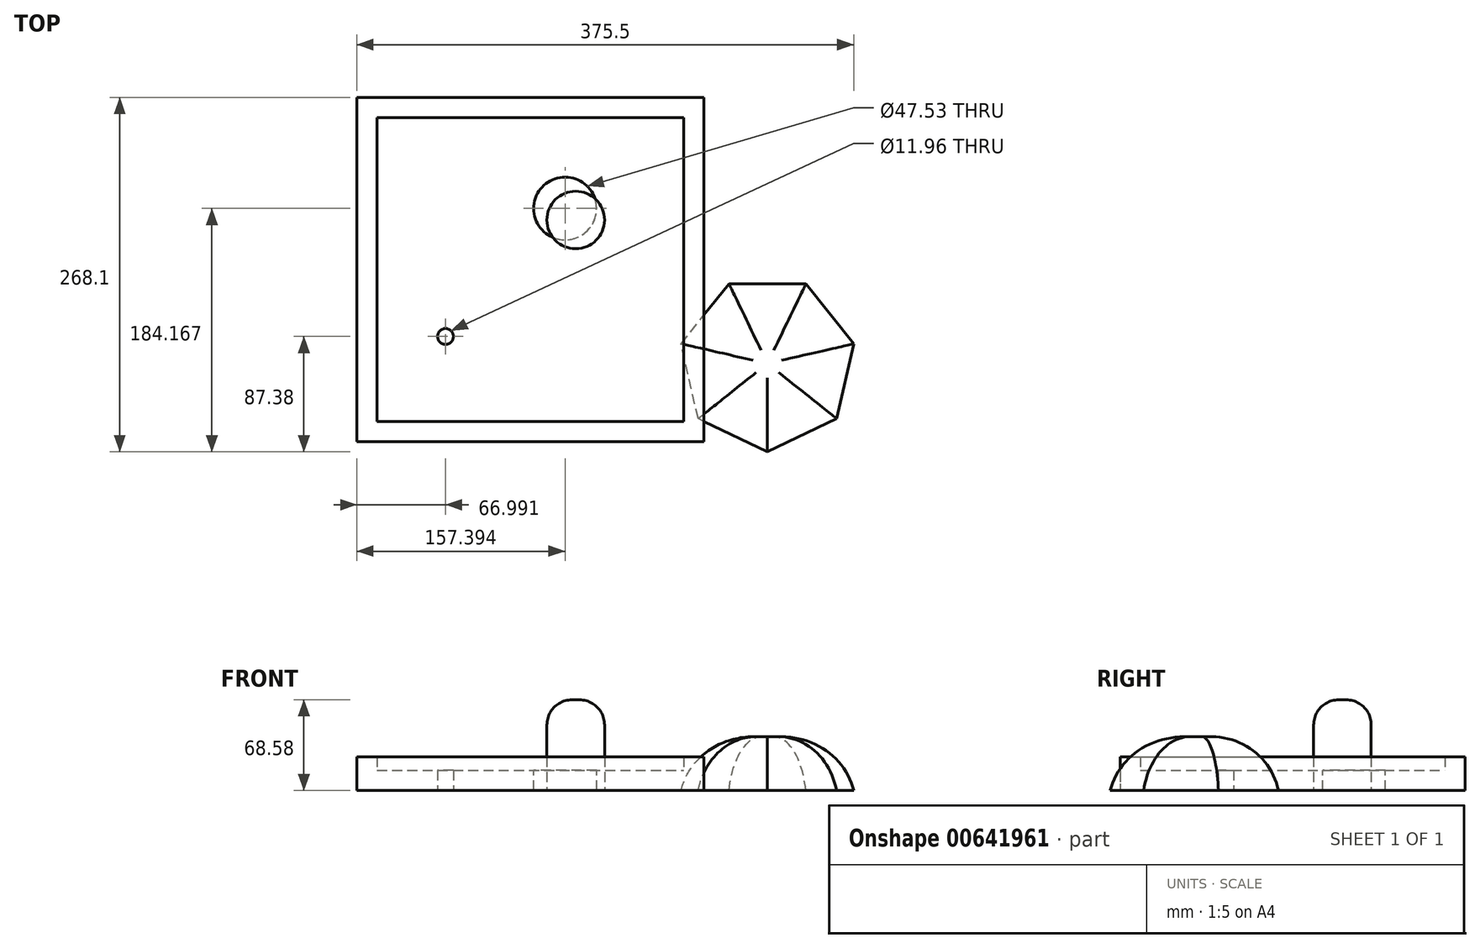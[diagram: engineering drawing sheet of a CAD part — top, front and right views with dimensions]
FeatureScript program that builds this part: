
annotation { "Feature Type Name" : "Feature", "Feature Type Description" : "" }
export const myFeature = defineFeature(function(context is Context, id is Id, definition is map)
    precondition{}
    {
        {
            var Q0;
            Q0=qCreatedBy(makeId("Top.planeOp"),FACE);
            var sketch = newSketch(context, id + "F0", { "sketchPlane" : qUnion([Q0])});
            skCircle(sketch, "E0", {"center": v(-54.37, 0) * mm, "radius": 55.17 * mm});
            skSolve(sketch);
        }
        {
            var Q0;
            Q0=makeQuery(id+"F0.imprint","IMPRINT",FACE,{"disambiguationData":[TD([[makeQuery(id+"F0.imprint","IMPRINT",EDGE,{"derivedFrom":sQuery(id+"F0.wireOp",EDGE,"E0")}),1.0]])]});
            var Q1;
            Q1=sQuery(id+"F0.wireOp",EDGE,"E0");
            extrude(context, id + "F1", {"entities" : qUnion([Q0]), "bodyType" : ToolBodyType.SURFACE, "surfaceEntities" : qUnion([Q1]), "depth" : 71.37 * mm});
        }
        {
            var Q0;
            Q0=qCreatedBy(makeId("Top.planeOp"),FACE);
            var sketch = newSketch(context, id + "F2", { "sketchPlane" : qUnion([Q0])});
            skLineSegment(sketch, "E1.bottom", {"start": v(-115.64, -136.24) * mm, "end": v(146.72, -136.24) * mm});
            skLineSegment(sketch, "E1.top", {"start": v(-115.64, 124.25) * mm, "end": v(146.72, 124.25) * mm});
            skLineSegment(sketch, "E1.left", {"start": v(-115.64, -136.24) * mm, "end": v(-115.64, 124.25) * mm});
            skLineSegment(sketch, "E1.right", {"start": v(146.72, -136.24) * mm, "end": v(146.72, 124.25) * mm});
            skSolve(sketch);
        }
        {
            var Q0;
            Q0=makeQuery(id+"F2.imprint","IMPRINT",FACE,{"disambiguationData":[TD([[makeQuery(id+"F2.imprint","IMPRINT",EDGE,{"derivedFrom":sQuery(id+"F2.wireOp",EDGE,"E1.bottom")}),1.0]])]});
            extrude(context, id + "F3", {"entities" : qUnion([Q0]), "depth" : 25.4 * mm});
        }
        {
            var Q0;
            Q0=qCreatedBy(makeId("Top.planeOp"),FACE);
            var sketch = newSketch(context, id + "F4", { "sketchPlane" : qUnion([Q0])});
            skCircle(sketch, "E2", {"center": v(-48.65, -56.47) * mm, "radius": 47.53 * mm});
            skSolve(sketch);
        }
        {
            var Q0;
            Q0=sQuery(id+"F4.wireOp",EDGE,"E2");
            extrude(context, id + "F5", {"bodyType" : ToolBodyType.SURFACE, "surfaceEntities" : qUnion([Q0]), "depth" : 160.02 * mm, "offsetDistance" : 25.4 * mm});
        }
        {
            var Q0;
            Q0=makeQuery(id+"F3.opExtrude","CAP_FACE",FACE,{"disambiguationData":[OSD([sQuery(id+"F2.wireOp",EDGE,"E1.bottom"),sQuery(id+"F2.wireOp",EDGE,"E1.top"),sQuery(id+"F2.wireOp",EDGE,"E1.left"),sQuery(id+"F2.wireOp",EDGE,"E1.right")])],"isStart":false});
            shell(context, id + "F6", {"entities" : qUnion([Q0]), "thickness" : 15.24 * mm});
        }
        {
            var Q0;
            Q0=makeQuery(id+"F6.opShell","OFFSET_FACE",FACE,{"disambiguationData":[OSD([sQuery(id+"F2.wireOp",EDGE,"E1.bottom"),sQuery(id+"F2.wireOp",EDGE,"E1.top"),sQuery(id+"F2.wireOp",EDGE,"E1.left"),sQuery(id+"F2.wireOp",EDGE,"E1.right")])]});
            var sketch = newSketch(context, id + "F7", { "sketchPlane" : qUnion([Q0])});
            skPoint(sketch, "E3", {"position": v(41.75, 40.32) * mm});
            skSolve(sketch);
        }
        {
            var Q0;
            Q0=sQuery(id+"F7.wireOp",VERTEX,"E3");
            var Q1;
            Q1=makeQuery(id+"F3.opExtrude","SWEPT_BODY",BODY,{"disambiguationData":[OSD([sQuery(id+"F2.wireOp",EDGE,"E1.bottom"),sQuery(id+"F2.wireOp",EDGE,"E1.top"),sQuery(id+"F2.wireOp",EDGE,"E1.left"),sQuery(id+"F2.wireOp",EDGE,"E1.right")])]});
            hole(context, id + "F8", {"style" : HoleStyle.SIMPLE, "endStyle" : HoleEndStyle.THROUGH, "holeDiameter" : 47.53 * mm, "majorDiameter" : 6.35 * mm, "isTappedThrough" : true, "tappedDepth" : 12.7 * mm, "tapClearance" : 3, "locations" : qUnion([Q0]), "scope" : qUnion([Q1])});
        }
        {
            var Q0;
            Q0=qCreatedBy(makeId("Top.planeOp"),FACE);
            var sketch = newSketch(context, id + "F9", { "sketchPlane" : qUnion([Q0])});
            skCircle(sketch, "E4", {"center": v(49.77, 31.6) * mm, "radius": 21.77 * mm});
            skSolve(sketch);
        }
        {
            var Q0;
            Q0=makeQuery(id+"F9.imprint","IMPRINT",FACE,{"disambiguationData":[TD([[makeQuery(id+"F9.imprint","IMPRINT",EDGE,{"derivedFrom":sQuery(id+"F9.wireOp",EDGE,"E4")}),1.0]])]});
            extrude(context, id + "F10", {"entities" : qUnion([Q0]), "depth" : 68.58 * mm, "offsetDistance" : 25.4 * mm});
        }
        {
            var Q0;
            Q0=makeQuery(id+"F10.opExtrude","CAP_EDGE",EDGE,{"disambiguationData":[OSD([sQuery(id+"F9.wireOp",EDGE,"E4")])],"isStart":false});
            fillet(context, id + "F11", {"entities" : qUnion([Q0]), "radius" : 19 * mm, "tangentPropagation" : true, "allowEdgeOverflow" : false});
        }
        {
            var Q0;
            Q0=qCreatedBy(makeId("Top.planeOp"),FACE);
            var sketch = newSketch(context, id + "F12", { "sketchPlane" : qUnion([Q0])});
            skCircle(sketch, "E5.cCircle", {"center": v(194.64, -76.95) * mm, "radius": 60.28 * mm, "construction": true});
            skLineSegment(sketch, "E5.0", {"start": v(165.6, -16.67) * mm, "end": v(223.67, -16.67) * mm});
            skLineSegment(sketch, "E5.1", {"start": v(223.67, -16.67) * mm, "end": v(259.86, -62.06) * mm});
            skLineSegment(sketch, "E5.2", {"start": v(259.86, -62.06) * mm, "end": v(246.94, -118.66) * mm});
            skLineSegment(sketch, "E5.3", {"start": v(246.94, -118.66) * mm, "end": v(194.64, -143.85) * mm});
            skLineSegment(sketch, "E5.4", {"start": v(194.64, -143.85) * mm, "end": v(142.33, -118.66) * mm});
            skLineSegment(sketch, "E5.5", {"start": v(142.33, -118.66) * mm, "end": v(129.41, -62.06) * mm});
            skLineSegment(sketch, "E5.6", {"start": v(129.41, -62.06) * mm, "end": v(165.6, -16.67) * mm});
            skPoint(sketch, "E5.0.midPoint", {"position": v(194.64, -16.67) * mm});
            skSolve(sketch);
        }
        {
            var Q0;
            Q0=makeQuery(id+"F12.imprint","IMPRINT",FACE,{"disambiguationData":[TD([[makeQuery(id+"F12.imprint","IMPRINT",EDGE,{"derivedFrom":sQuery(id+"F12.wireOp",EDGE,"E5.0")}),-1.0]])]});
            extrude(context, id + "F13", {"entities" : qUnion([Q0]), "depth" : 40.64 * mm, "offsetDistance" : 25.4 * mm});
        }
        {
            var Q0;
            Q0=makeQuery(id+"F13.opExtrude","CAP_FACE",FACE,{"disambiguationData":[OSD([sQuery(id+"F12.wireOp",EDGE,"E5.0"),sQuery(id+"F12.wireOp",EDGE,"E5.1"),sQuery(id+"F12.wireOp",EDGE,"E5.2"),sQuery(id+"F12.wireOp",EDGE,"E5.3"),sQuery(id+"F12.wireOp",EDGE,"E5.4"),sQuery(id+"F12.wireOp",EDGE,"E5.5"),sQuery(id+"F12.wireOp",EDGE,"E5.6")])],"isStart":false});
            fillet(context, id + "F14", {"entities" : qUnion([Q0]), "radius" : 51.5 * mm, "tangentPropagation" : true, "allowEdgeOverflow" : false});
        }
        {
            var Q0;
            Q0=sQuery(id+"F4.wireOp",VERTEX,"E2.center");
            var Q1;
            Q1=makeQuery(id+"F3.opExtrude","SWEPT_BODY",BODY,{"disambiguationData":[OSD([sQuery(id+"F2.wireOp",EDGE,"E1.bottom"),sQuery(id+"F2.wireOp",EDGE,"E1.top"),sQuery(id+"F2.wireOp",EDGE,"E1.left"),sQuery(id+"F2.wireOp",EDGE,"E1.right")])]});
            hole(context, id + "F15", {"style" : HoleStyle.SIMPLE, "endStyle" : HoleEndStyle.THROUGH, "oppositeDirection" : true, "holeDiameter" : 11.96 * mm, "majorDiameter" : 6.35 * mm, "isTappedThrough" : true, "tappedDepth" : 12.7 * mm, "tapClearance" : 3, "locations" : qUnion([Q0]), "scope" : qUnion([Q1])});
        }
    });
